# Revit family: 00-7902-05-05
name_source: partatom
category: Luminarias
revit_build: Autodesk Revit 2017 (Build: 20160225_1515(x64)
units: mm (PartAtom-declared; Revit-internal decimal feet)

## family parameters
Anfitrión = Cara
Compartido = Sí
Corte con vacíos al cargar = No
Cota de conector redondo = Diámetro de uso
Número OmniClass = 23.80.70.00
Origen de luz = No
Punto de cálculo de habitación = No
Tipo de pieza = Normal
Título OmniClass = Lighting

## types (1)
- 00-7902-05-05
    Acabado = Negro
    CRI = 90
    Carga aparente = 0 VA
    Catálogo = Decorative
    CodigoGubimclass = 50.60.50.20
    CodigoOmniclass = 21-04 50 40
    CodigoUniclass2015 = EF_70_80
    CodigoUniformat2010 = D5040
    DescripcionGubimclass = Iluminación interior
    DescripcionOmniclass = Lighting
    DescripcionUniclass2015 = Lighting
    DescripcionUniformat2010 = Lighting
    EAN13 = 8435575323728
    Eficiencia energética = LED A++
    Elevación por defecto = 1000 mm  [stored 3.28084 ft]
    Etiqueta V/f = 100-240V/50-60Hz
    Fabricante = LEDS C4
    Familia = Punto Multiple Surface
    FechaVersion = Julio 2020
    Ficha = http://files.leds-c4.com
    Fotometría = http://files.leds-c4.com
    IMC = http://files.leds-c4.com
    IP = IP20
    IfcExportAs = IfcLightFixture
IfcLightFixture
    IfcExportType = NOTDEFINED
    Imagen web = http://files.leds-c4.com
    LDT = http://files.leds-c4.com
    Lumenes reales (lm) = 625
    Material = Aluminio
    Peso neto (KG) = 1.64
    Producto descatalogado = Catalogado ES
    Rayo de luz = EXTRA MEDIUM
    Referencia = 00-7902-05-05
    Temperatura color led (K) = Blanco cálido - 3000K
    Tender text (Castellano) = LEDS C4
Punto Multiple Surface
00-7902-05-05

Colgante de uso interior para iluminar hacia abajo. 
Material estructura: Aluminio. Acabado estructura: Negro. Garantía: 5 Años.

Peso neto del producto (Kg): 1.640
Longitud del producto (mm): 5000
Anchura o diámetro del producto (mm): 140
Altura del producto (mm): 1200
Ø del agujero para empotrar (mm): 60

Clase 1. IP: IP20. LED. Nº de portalámparas o Leds: 5. Marca del LED: CREE. Marca del Driver: HEP. Potencia máxima de la fuente de luz: 18.5W. Temperatura de color: Blanco cálido - 3000K. Índice de reproducción cromática: 90. Steps Mac Adam: 3. Diámetro máximo de la bombilla que admite la luminaria: 50.000h L80B20. UGR:  8.3. Riesgo fotobiológico: RG2. Flujo real (lm): 625. Lm/W reales: 26. Rango de voltaje/frecuencia: 100-240/50-60Hz. Voltaje: 3. Equipo incluido: Si, electrónico. Potencia total: 24.3. Factor de potencia: 0.90.
    Tender text (English) = LEDS C4
Punto Multiple Surface
00-7902-05-05

Pendant for indoor use. 

For downlighting. Structure material: Aluminium. Structure finish: Black. Warranty: 5 Years.

Product net weight (Kg): 1.640
Product length (mm): 5000
Product width or diameter (mm): 140
Product height (mm): 1200
Ø of the hole for recessing (mm): 60

Class 1. IP: IP20. LED. No. of lampholders or LEDs: 5. LED brand: CREE. Driver brand: HEP. Maximum power of light source: 18.5W. Colour temperature: LED warm-white 3000K. Colour rendering index: 90. MacAdam Steps: 3. Maximum diameter of luminaire bulb: 50.000h L80B20. UGR:  8.3. Photobiological risk: RG2. Real flux (lm): 625. Lm/Real W: 26. Voltage and frequency range: 100-240/50-60Hz. Voltage: 3. Gear included: Yes, electronic. Total power: 24.3. Power factor: 0.90.
    Tipo = Colgante
    Vatios (W) = 24.3
    Versión = v1

note: [stored X ft] marks values corroborated as IEEE doubles in the binary element streams (Revit-internal decimal feet)
